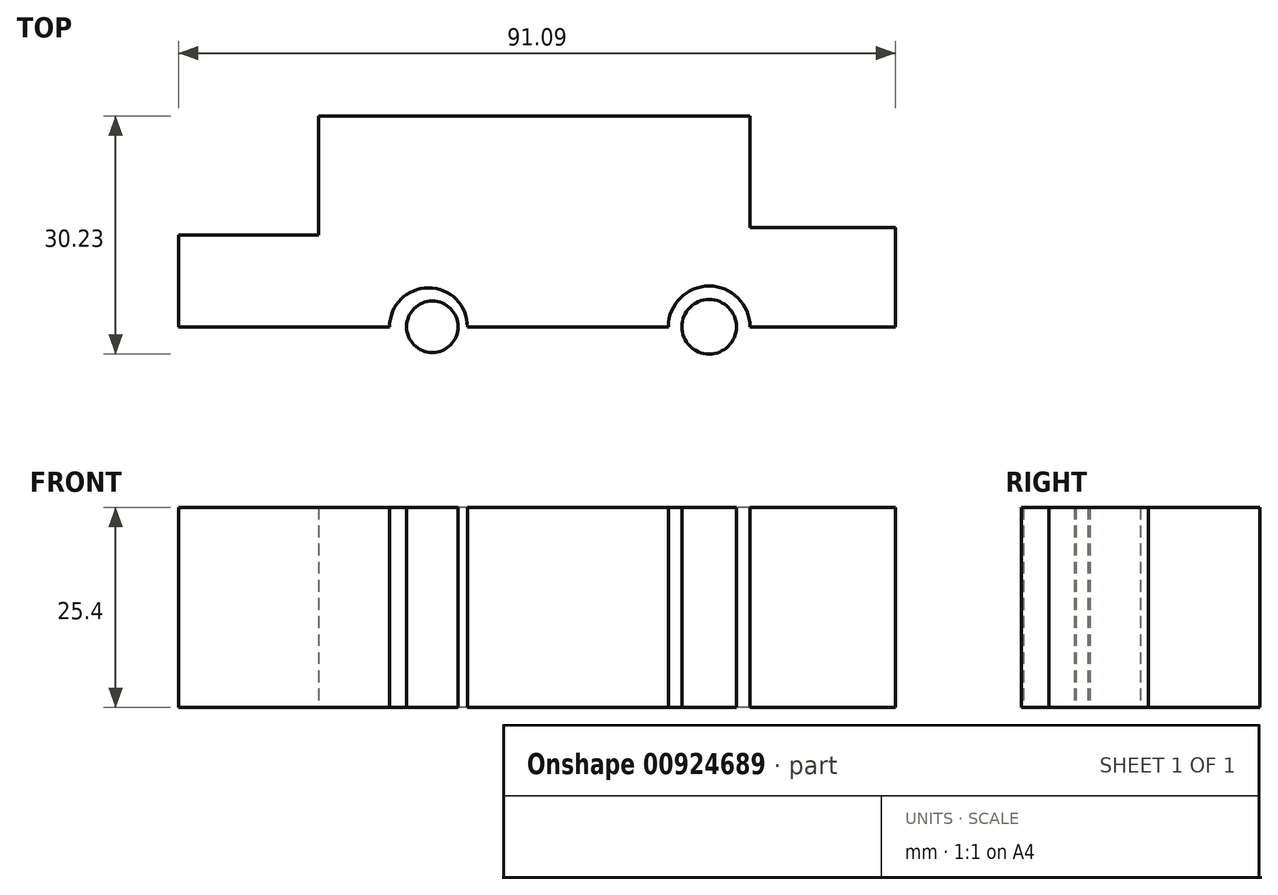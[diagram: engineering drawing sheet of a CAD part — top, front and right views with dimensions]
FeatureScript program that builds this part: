
annotation { "Feature Type Name" : "Feature", "Feature Type Description" : "" }
export const myFeature = defineFeature(function(context is Context, id is Id, definition is map)
    precondition{}
    {
        {
            var Q0;
            Q0=qCreatedBy(makeId("Top.planeOp"),FACE);
            var sketch = newSketch(context, id + "F0", { "sketchPlane" : qUnion([Q0])});
            skLineSegment(sketch, "E0", {"start": v(25.57, 26.77) * mm, "end": v(-29.2, 26.77) * mm});
            skLineSegment(sketch, "E1", {"start": v(-29.2, 26.77) * mm, "end": v(-29.2, 11.64) * mm});
            skLineSegment(sketch, "E2", {"start": v(25.57, 12.62) * mm, "end": v(25.57, 26.77) * mm});
            skLineSegment(sketch, "E3", {"start": v(-47, 0) * mm, "end": v(-47, 11.64) * mm});
            skLineSegment(sketch, "E4", {"start": v(-29.2, 11.64) * mm, "end": v(-47, 11.64) * mm});
            skLineSegment(sketch, "E5", {"start": v(44.08, 12.62) * mm, "end": v(44.08, 12.62) * mm});
            skLineSegment(sketch, "E6", {"start": v(44.08, 12.62) * mm, "end": v(25.57, 12.62) * mm});
            skLineSegment(sketch, "E7", {"start": v(44.08, 0) * mm, "end": v(44.08, 12.62) * mm});
            skLineSegment(sketch, "E8", {"start": v(-29.2, 0) * mm, "end": v(-29.2, 0) * mm});
            skLineSegment(sketch, "E9", {"start": v(-29.2, 0) * mm, "end": v(-47, 0) * mm});
            skCircle(sketch, "E10", {"center": v(20.39, 0) * mm, "radius": 5.18 * mm});
            skCircle(sketch, "E11", {"center": v(-15.26, 0) * mm, "radius": 4.95 * mm});
            skLineSegment(sketch, "E12", {"start": v(-15.26, 0) * mm, "end": v(-29.2, 0) * mm});
            skLineSegment(sketch, "E13", {"start": v(44.08, 0) * mm, "end": v(20.39, 0) * mm});
            skLineSegment(sketch, "E14", {"start": v(-15.26, 0) * mm, "end": v(20.39, 0) * mm});
            skSolve(sketch);
        }
        {
            var Q0;
            Q0=makeQuery(id+"F0.imprint","IMPRINT",FACE,{"disambiguationData":[TD([[makeQuery(id+"F0.imprint","IMPRINT",EDGE,{"derivedFrom":sQuery(id+"F0.wireOp",EDGE,"E0")}),1.0]])]});
            extrude(context, id + "F1", {"entities" : qUnion([Q0]), "depth" : 25.4 * mm, "offsetDistance" : 25.4 * mm});
        }
        {
            var Q0;
            Q0=qCreatedBy(makeId("Top.planeOp"),FACE);
            var sketch = newSketch(context, id + "F2", { "sketchPlane" : qUnion([Q0])});
            skCircle(sketch, "E15", {"center": v(-14.77, 0) * mm, "radius": 3.26 * mm});
            skCircle(sketch, "E16", {"center": v(20.39, 0) * mm, "radius": 3.46 * mm});
            skSolve(sketch);
        }
        {
            var Q0;
            Q0 = qSketchRegion(id + "F2", true);
            extrude(context, id + "F3", {"entities" : qUnion([Q0]), "depth" : 25.4 * mm, "offsetDistance" : 25.4 * mm});
        }
    });
